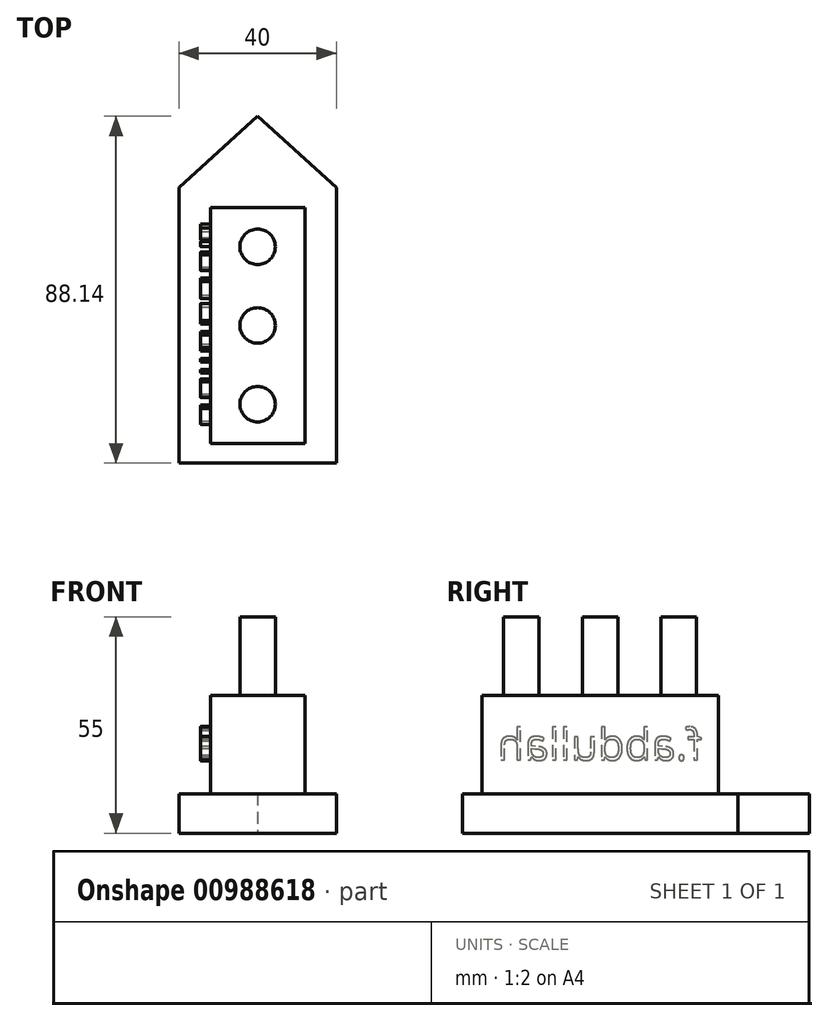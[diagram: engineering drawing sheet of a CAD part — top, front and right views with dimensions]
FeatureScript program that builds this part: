
annotation { "Feature Type Name" : "Feature", "Feature Type Description" : "" }
export const myFeature = defineFeature(function(context is Context, id is Id, definition is map)
    precondition{}
    {
        {
            var Q0;
            Q0=qCreatedBy(makeId("Top.planeOp"),FACE);
            var sketch = newSketch(context, id + "F0", { "sketchPlane" : qUnion([Q0])});
            skLineSegment(sketch, "E0", {"start": v(20, -35) * mm, "end": v(-20, -35) * mm});
            skLineSegment(sketch, "E1", {"start": v(-20, -35) * mm, "end": v(-20, 35) * mm});
            skLineSegment(sketch, "E2", {"start": v(-20, 35) * mm, "end": v(0, 53.14) * mm});
            skLineSegment(sketch, "E3", {"start": v(0, 53.14) * mm, "end": v(20, 35) * mm});
            skLineSegment(sketch, "E4", {"start": v(20, 35) * mm, "end": v(20, -35) * mm});
            skSolve(sketch);
        }
        {
            var Q0;
            Q0 = qSketchRegion(id + "F0", true);
            extrude(context, id + "F1", {"entities" : qUnion([Q0]), "depth" : 10 * mm, "offsetDistance" : 25 * mm});
        }
        {
            var Q0;
            Q0=makeQuery(id+"F1.opExtrude","CAP_FACE",FACE,{"disambiguationData":[OSD([sQuery(id+"F0.wireOp",EDGE,"E0"),sQuery(id+"F0.wireOp",EDGE,"E1"),sQuery(id+"F0.wireOp",EDGE,"E2"),sQuery(id+"F0.wireOp",EDGE,"E3"),sQuery(id+"F0.wireOp",EDGE,"E4")])],"isStart":false});
            var sketch = newSketch(context, id + "F2", { "sketchPlane" : qUnion([Q0])});
            skLineSegment(sketch, "E5", {"start": v(-12, 30) * mm, "end": v(-12, -30) * mm});
            skLineSegment(sketch, "E6", {"start": v(-12, -30) * mm, "end": v(12, -30) * mm});
            skLineSegment(sketch, "E7", {"start": v(12, -30) * mm, "end": v(12, 30) * mm});
            skLineSegment(sketch, "E8", {"start": v(12, 30) * mm, "end": v(-12, 30) * mm});
            skSolve(sketch);
        }
        {
            var Q0;
            Q0=makeQuery(id+"F2.imprint","IMPRINT",FACE,{"disambiguationData":[TD([[makeQuery(id+"F2.imprint","IMPRINT",EDGE,{"derivedFrom":sQuery(id+"F2.wireOp",EDGE,"E5")}),1.0]])]});
            extrude(context, id + "F3", {"entities" : qUnion([Q0]), "operationType" : NewBodyOperationType.ADD, "depth" : 25 * mm, "offsetDistance" : 25 * mm});
        }
        {
            var Q0;
            Q0=makeQuery(id+"F3.opExtrude","CAP_FACE",FACE,{"disambiguationData":[OSD([sQuery(id+"F2.wireOp",EDGE,"E5"),sQuery(id+"F2.wireOp",EDGE,"E6"),sQuery(id+"F2.wireOp",EDGE,"E7"),sQuery(id+"F2.wireOp",EDGE,"E8")])],"isStart":false});
            var sketch = newSketch(context, id + "F4", { "sketchPlane" : qUnion([Q0])});
            skCircle(sketch, "E9", {"center": v(0, -20) * mm, "radius": 4.5 * mm});
            skCircle(sketch, "E10", {"center": v(0, 0) * mm, "radius": 4.5 * mm});
            skCircle(sketch, "E11", {"center": v(0, 20) * mm, "radius": 4.5 * mm});
            skSolve(sketch);
        }
        {
            var Q0;
            Q0 = qSketchRegion(id + "F4", true);
            extrude(context, id + "F5", {"entities" : qUnion([Q0]), "operationType" : NewBodyOperationType.ADD, "depth" : 20 * mm, "offsetDistance" : 25 * mm});
        }
        {
            var Q0;
            Q0=makeQuery(id+"F3.opExtrude","SWEPT_FACE",FACE,{"disambiguationData":[OSD([sQuery(id+"F2.wireOp",EDGE,"E5")])]});
            var sketch = newSketch(context, id + "F6", { "sketchPlane" : qUnion([Q0])});
            skText(sketch, "E12", { "text": "f.abdullah", "fontName": "OpenSans-Regular.ttf"});
            const initialGuessF6  = {"E12": [-0.02592, 0.01857, 1, 0, 0.008]};
            skSetInitialGuess(sketch, initialGuessF6);
            skSolve(sketch);
        }
        {
            var Q0;
            Q0 = qSketchRegion(id + "F6", true);
            extrude(context, id + "F7", {"entities" : qUnion([Q0]), "operationType" : NewBodyOperationType.ADD, "depth" : 2.5 * mm, "offsetDistance" : 25 * mm});
        }
    });
